# Revit family: Reece_Waste_Mizu_Drift_Bottle Trap_Removable Base
name_source: partatom
category: Plumbing Fixtures
revit_build: Autodesk Revit 2018 (Build: 20180329_1100(x64)
units: mm (PartAtom-declared; Revit-internal decimal feet)

## family parameters
Cut with Voids When Loaded = Yes
Host = Face
Part Type = Normal
Room Calculation Point = Yes
Round Connector Dimension = Use Diameter
Shared = Yes

## types (1)
- Chrome
    Default Elevation = 0 mm  [stored 0 ft]
    Description = Mizu Drift Bottle Trap with Removable Base Chrome
    Disclaimer = THIS FILE IS THE PROPERTY OF THE REECE GROUP. IT MAY NOT BE REPRODUCED, REVERSE-ENGINEERED OR MODIFIED. ANY REPUBLICATION, TRANSMISSION OR DISTRIBUTION FOR THE PURPOSE OF COMMERCIALLY EXPLOITING THE FILES IS PROHIBITED.
    Keynote = Product #2261125, Reece_Waste_Mizu_Drift_Bottle Trap_Removable Base - Chrome
    Manufacturer = Mizu
    Model = Drift
    Reece_Detail_Additional = Removable Base
    Reece_Detail_Disclaimer = THIS FILE IS THE PROPERTY OF THE REECE GROUP. IT MAY NOT BE REPRODUCED, REVERSE-ENGINEERED OR MODIFIED. ANY REPUBLICATION, TRANSMISSION OR DISTRIBUTION FOR THE PURPOSE OF COMMERCIALLY EXPLOITING THE FILES IS PROHIBITED.
    Reece_Material_Main = Reece_Brass_Chrome
    Reece_Material_Secondary = Reece_Metal_Steel
    Reece_Overall_Width = 584 mm
    Reece_Product_Brand = Mizu
    Reece_Product_Description = Mizu Drift Bottle Trap with Removable Base Chrome
    Reece_Product_Mount = Wall Mounted
    Reece_Product_Number = 2261125
    Reece_Product_Sub Brand = Drift
    Reece_Product_Type = Bottle Trap
    Reece_Product_Web Page = www.reece.com.au/product/-2261125
    Reece_Waste_Outlet = 40 mm
    Type Comments = Bottle Trap
    URL = www.reece.com.au/product/-2261125

note: [stored X ft] marks values corroborated as IEEE doubles in the binary element streams (Revit-internal decimal feet)

## geometry (parser evidence)
native form markers: Sweep x3
no freeform markers — native parametric forms only
